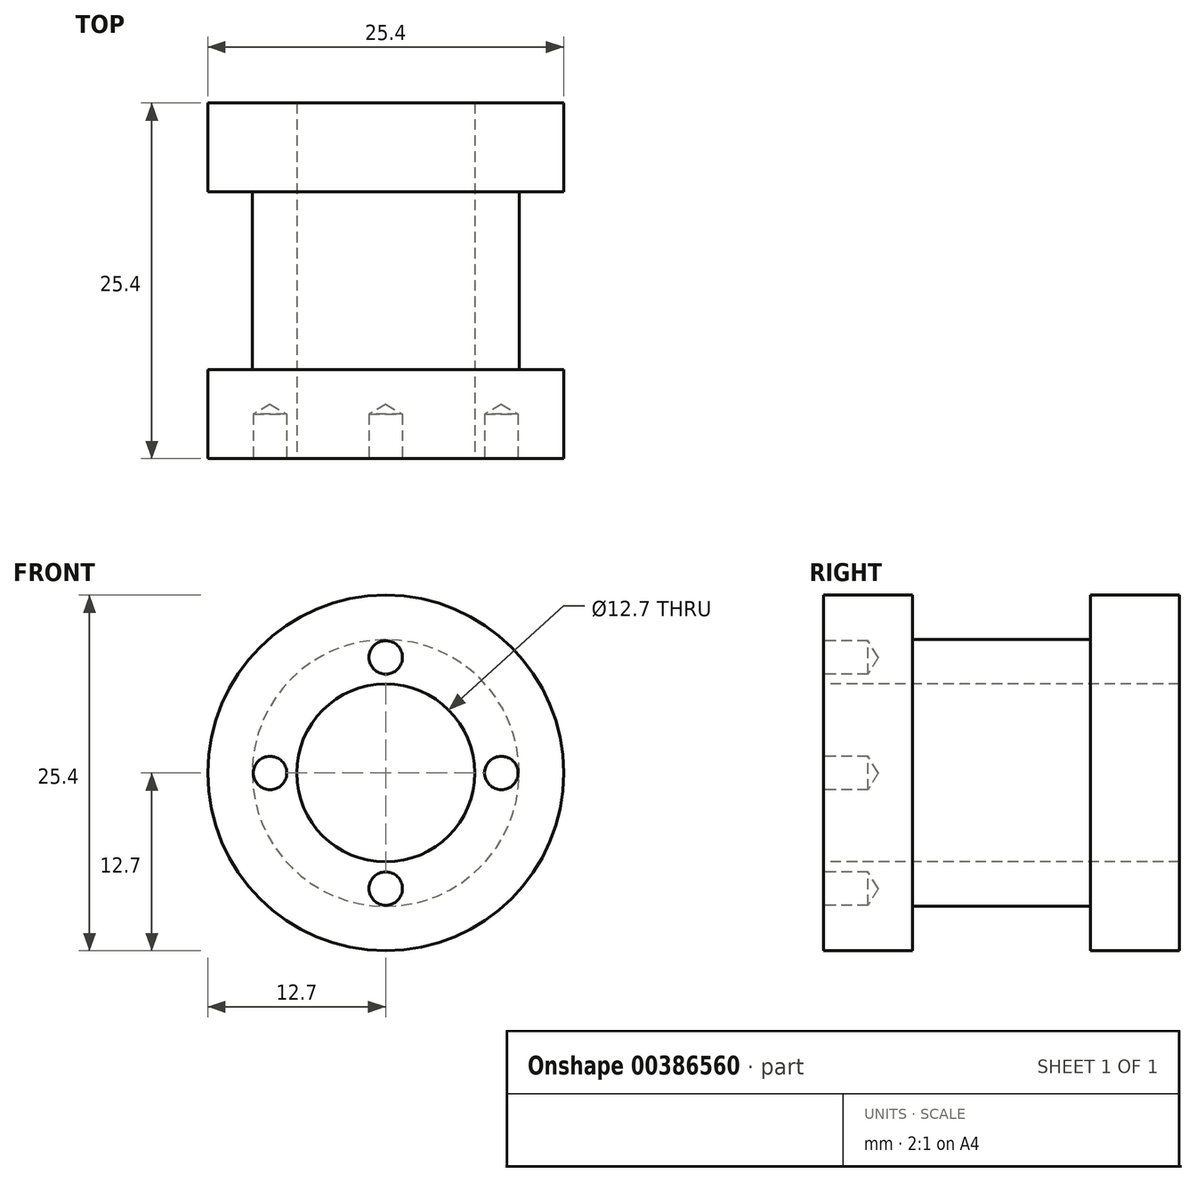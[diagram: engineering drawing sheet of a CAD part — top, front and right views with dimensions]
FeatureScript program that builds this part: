
annotation { "Feature Type Name" : "Feature", "Feature Type Description" : "" }
export const myFeature = defineFeature(function(context is Context, id is Id, definition is map)
    precondition{}
    {
        {
            var Q0;
            Q0=qCreatedBy(makeId("Front.planeOp"),FACE);
            var sketch = newSketch(context, id + "F0", { "sketchPlane" : qUnion([Q0])});
            skCircle(sketch, "E0", {"center": v(0, 0) * mm, "radius": 12.7 * mm});
            skSolve(sketch);
        }
        {
            var Q0;
            Q0 = qSketchRegion(id + "F0", true);
            extrude(context, id + "F1", {"entities" : qUnion([Q0]), "depth" : 6.35 * mm});
        }
        {
            var Q0;
            Q0=makeQuery(id+"F1.opExtrude","CAP_FACE",FACE,{"disambiguationData":[OSD([sQuery(id+"F0.wireOp",EDGE,"E0")])],"isStart":false});
            var sketch = newSketch(context, id + "F2", { "sketchPlane" : qUnion([Q0])});
            skCircle(sketch, "E1", {"center": v(0, 0) * mm, "radius": 9.53 * mm});
            skSolve(sketch);
        }
        {
            var Q0;
            Q0 = qSketchRegion(id + "F2", true);
            extrude(context, id + "F3", {"entities" : qUnion([Q0]), "operationType" : NewBodyOperationType.ADD, "depth" : 12.7 * mm});
        }
        {
            var Q0;
            Q0=makeQuery(id+"F3.opExtrude","CAP_FACE",FACE,{"disambiguationData":[OSD([sQuery(id+"F2.wireOp",EDGE,"E1")])],"isStart":false});
            var sketch = newSketch(context, id + "F4", { "sketchPlane" : qUnion([Q0])});
            skCircle(sketch, "E2", {"center": v(0, 0) * mm, "radius": 12.7 * mm});
            skSolve(sketch);
        }
        {
            var Q0;
            Q0 = qSketchRegion(id + "F4", true);
            extrude(context, id + "F5", {"entities" : qUnion([Q0]), "operationType" : NewBodyOperationType.ADD, "depth" : 6.35 * mm});
        }
        {
            var Q0;
            Q0=makeQuery(id+"F5.opExtrude","CAP_FACE",FACE,{"disambiguationData":[OSD([sQuery(id+"F4.wireOp",EDGE,"E2")])],"isStart":false});
            var sketch = newSketch(context, id + "F6", { "sketchPlane" : qUnion([Q0])});
            skPoint(sketch, "E3", {"position": v(-8.26, 0) * mm});
            skPoint(sketch, "E4", {"position": v(8.26, 0) * mm});
            skPoint(sketch, "E5", {"position": v(0, 8.26) * mm});
            skPoint(sketch, "E6", {"position": v(0, -8.26) * mm});
            skSolve(sketch);
        }
        {
            var Q0;
            Q0=sQuery(id+"F6.wireOp",VERTEX,"E3");
            var Q1;
            Q1=sQuery(id+"F6.wireOp",VERTEX,"E5");
            var Q2;
            Q2=sQuery(id+"F6.wireOp",VERTEX,"E4");
            var Q3;
            Q3=sQuery(id+"F6.wireOp",VERTEX,"E6");
            var Q4;
            Q4=makeQuery(id+"F1.opExtrude","SWEPT_BODY",BODY,{"disambiguationData":[OSD([sQuery(id+"F0.wireOp",EDGE,"E0")])]});
            hole(context, id + "F7", {"style" : HoleStyle.SIMPLE, "endStyle" : HoleEndStyle.BLIND, "holeDiameter" : 2.4 * mm, "holeDepth" : 3.17 * mm, "isTappedThrough" : true, "tappedDepth" : 12.7 * mm, "tapClearance" : 3, "startFromSketch" : true, "locations" : qUnion([Q0, Q1, Q2, Q3]), "scope" : qUnion([Q4])});
        }
        {
            var Q0;
            Q0=makeQuery(id+"F5.opExtrude","CAP_FACE",FACE,{"disambiguationData":[OSD([sQuery(id+"F4.wireOp",EDGE,"E2")])],"isStart":false});
            var sketch = newSketch(context, id + "F8", { "sketchPlane" : qUnion([Q0])});
            skPoint(sketch, "E7", {"position": v(0, 0) * mm});
            skSolve(sketch);
        }
        {
            var Q0;
            Q0=sQuery(id+"F8.wireOp",VERTEX,"E7");
            var Q1;
            Q1=makeQuery(id+"F1.opExtrude","SWEPT_BODY",BODY,{"disambiguationData":[OSD([sQuery(id+"F0.wireOp",EDGE,"E0")])]});
            hole(context, id + "F9", {"style" : HoleStyle.SIMPLE, "endStyle" : HoleEndStyle.THROUGH, "holeDiameter" : 12.7 * mm, "isTappedThrough" : true, "tappedDepth" : 12.7 * mm, "tapClearance" : 3, "startFromSketch" : true, "locations" : qUnion([Q0]), "scope" : qUnion([Q1])});
        }
    });
